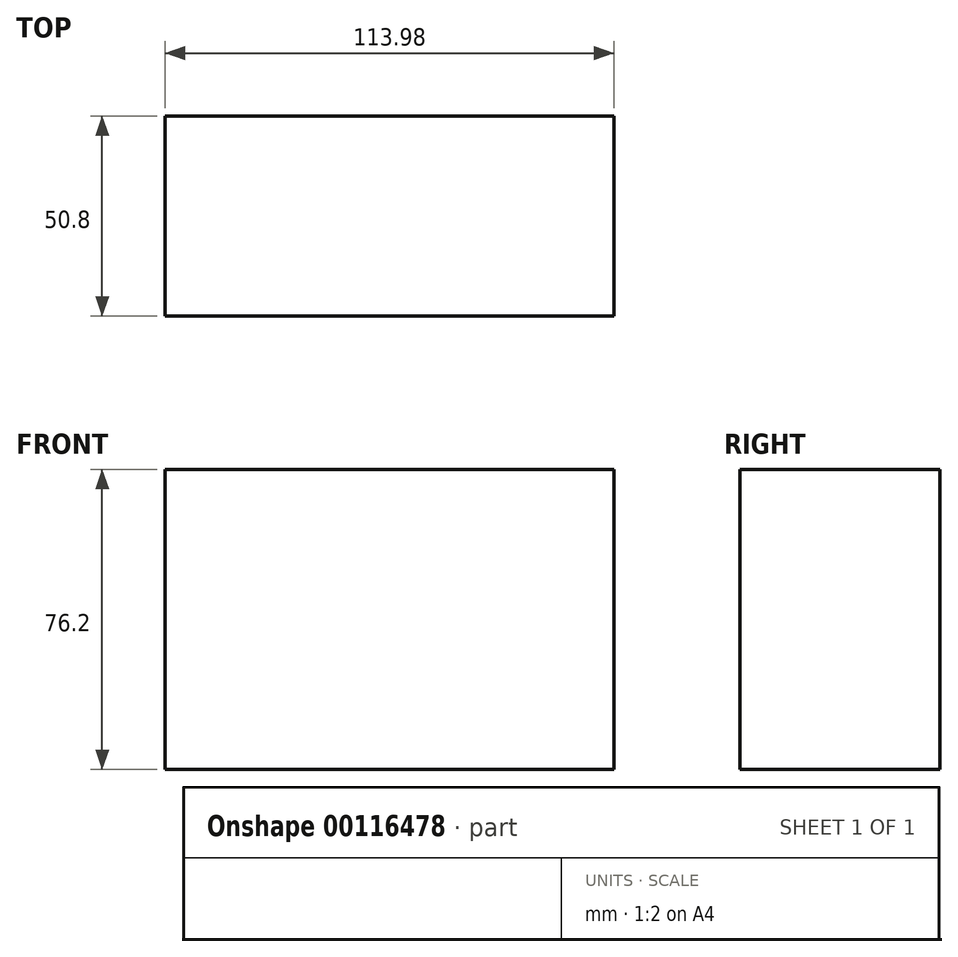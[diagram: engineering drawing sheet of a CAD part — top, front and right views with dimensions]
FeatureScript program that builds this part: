
annotation { "Feature Type Name" : "Feature", "Feature Type Description" : "" }
export const myFeature = defineFeature(function(context is Context, id is Id, definition is map)
    precondition{}
    {
        {
            var Q0;
            Q0=qCreatedBy(makeId("Front.planeOp"),FACE);
            var sketch = newSketch(context, id + "F0", { "sketchPlane" : qUnion([Q0])});
            skLineSegment(sketch, "E0.bottom", {"start": v(57, 38.1) * mm, "end": v(-57, 38.1) * mm});
            skLineSegment(sketch, "E0.top", {"start": v(57, -38.1) * mm, "end": v(-57, -38.1) * mm});
            skLineSegment(sketch, "E0.left", {"start": v(57, 38.1) * mm, "end": v(57, -38.1) * mm});
            skLineSegment(sketch, "E0.right", {"start": v(-57, 38.1) * mm, "end": v(-57, -38.1) * mm});
            skPoint(sketch, "E0.middle", {"position": v(0, 0) * mm});
            skSolve(sketch);
        }
        {
            var Q0;
            Q0=makeQuery(id+"F0.imprint","IMPRINT",FACE,{"disambiguationData":[TD([[makeQuery(id+"F0.imprint","IMPRINT",EDGE,{"derivedFrom":sQuery(id+"F0.wireOp",EDGE,"E0.bottom")}),1.0]])]});
            extrude(context, id + "F1", {"entities" : qUnion([Q0]), "oppositeDirection" : true, "depth" : 50.8 * mm});
        }
        {
            var Q0;
            Q0=makeQuery(id+"F1.opExtrude","SWEPT_FACE",FACE,{"disambiguationData":[OSD([sQuery(id+"F0.wireOp",EDGE,"E0.left")])]});
            var sketch = newSketch(context, id + "F2", { "sketchPlane" : qUnion([Q0])});
            skCircle(sketch, "E1", {"center": v(27.78, 0) * mm, "radius": 7.94 * mm});
            skSolve(sketch);
        }
        {
            var Q0;
            Q0=sQuery(id+"F2.wireOp",EDGE,"E1");
            extrude(context, id + "F3", {"bodyType" : ToolBodyType.SURFACE, "surfaceEntities" : qUnion([Q0]), "oppositeDirection" : true, "depth" : 127 * mm});
        }
    });
